# Revit family: Versorgungskasten mit umlaufendem Kleberand
name_source: partatom
category: Sanitärinstallationen
units: mm (PartAtom-declared; Revit-internal decimal feet)

## family parameters
Arbeitsebenenbasiert = Nein
Beim Laden mit Abzugskörper schneiden = Nein
Bemaßung runder Anschluss = Durchmesser verwenden
Gemeinsam genutzt = Nein
Immer vertikal = Ja
Raumberechnungspunkt = Nein
Teiletyp = Normal

## types (1)
- Versorgungskasten mit umlaufendem Kleberand
    Abwasserrohrverbindung = Nein
    Baugruppenkennzeichen = D2030300
    HW-Verbindung = Nein
    KW-Verbindung = Ja
    Lüftungsverbindung = Nein
    RS_Manufacture = Resitec
    RS_dim001 = 5 mm  [stored 0.0164042 ft]
    RS_dimKstT = 150 mm
    RS_dimdoor403 = 403 mm  [stored 1.32218 ft]
    RS_dimllue1 = 1 mm  [stored 0.00328084 ft]
    RS_rdimra20 = 20 mm  [stored 0.0656168 ft]
    RS_s1 = 4 mm  [stored 0.0131234 ft]
    RS_s2 = 2 mm  [stored 0.00656168 ft]
    URL = https://www.resitec.ch
    V max = 230
    Vorgabe-Ansicht = 0 mm  [stored 0 ft]

note: [stored X ft] marks values corroborated as IEEE doubles in the binary element streams (Revit-internal decimal feet)

## geometry (parser evidence)
native form markers: Sweep x1
no freeform markers — native parametric forms only
